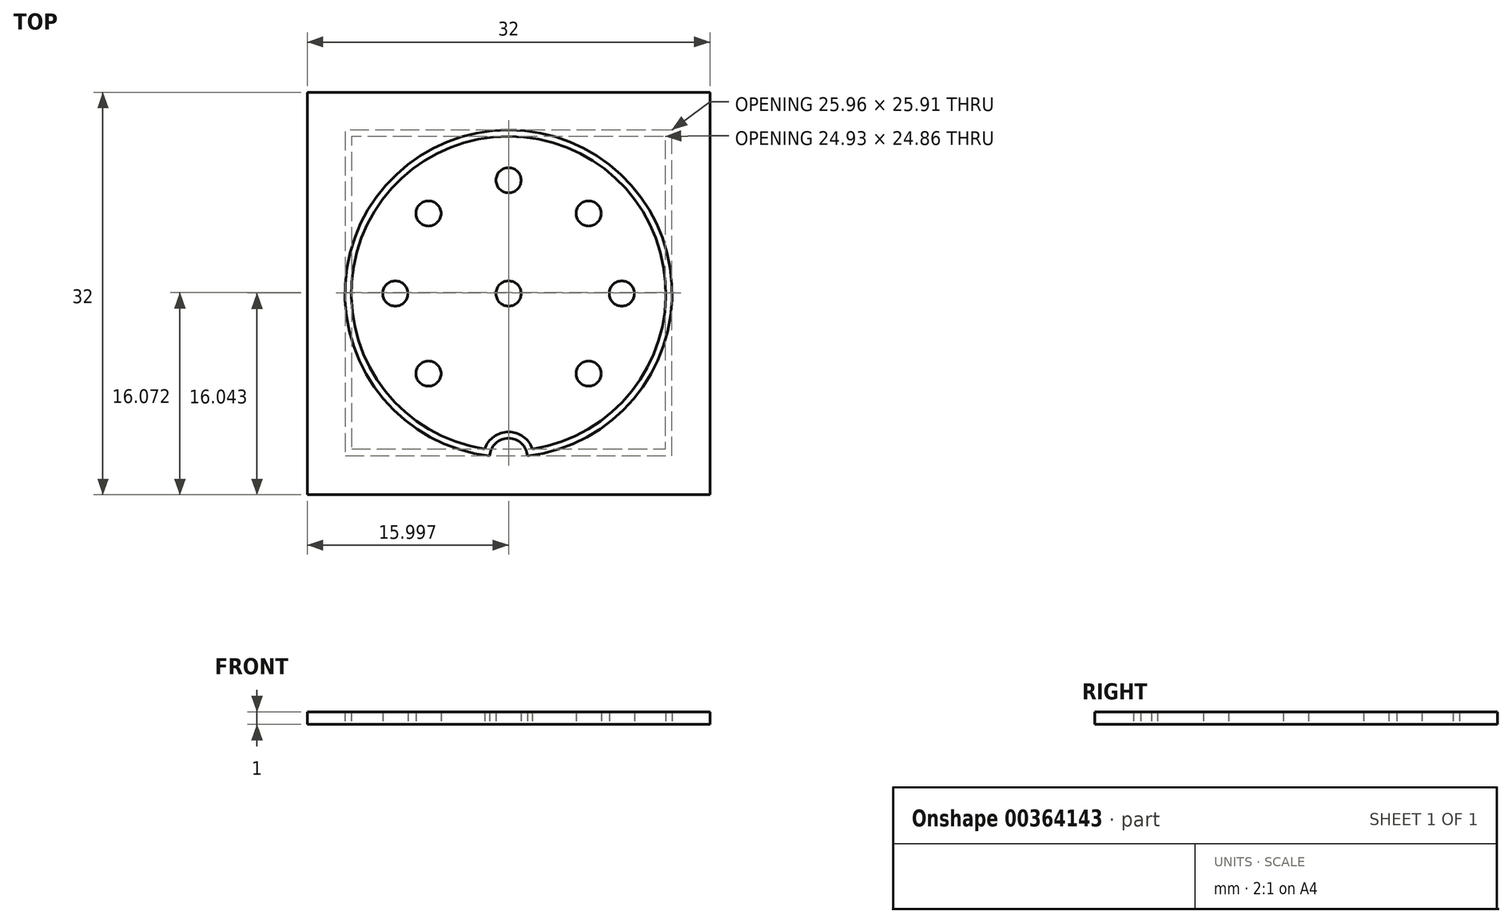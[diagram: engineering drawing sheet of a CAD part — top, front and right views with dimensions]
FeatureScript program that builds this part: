
annotation { "Feature Type Name" : "Feature", "Feature Type Description" : "" }
export const myFeature = defineFeature(function(context is Context, id is Id, definition is map)
    precondition{}
    {
        {
            var Q0;
            Q0=qCreatedBy(makeId("Top.planeOp"),FACE);
            var sketch = newSketch(context, id + "F0", { "sketchPlane" : qUnion([Q0])});
            skArc(sketch, "E0", {"start": v(1.9, -12.36) * mm, "mid": v(0, 12.5) * mm, "end": v(-1.9, -12.36) * mm});
            skCircle(sketch, "E1", {"center": v(0, 9) * mm, "radius": 1 * mm});
            skCircle(sketch, "E2", {"center": v(-9, 0) * mm, "radius": 1 * mm});
            skCircle(sketch, "E3", {"center": v(9, 0) * mm, "radius": 1 * mm});
            skLineSegment(sketch, "E4", {"start": v(0, 0) * mm, "end": v(0, 0) * mm});
            skCircle(sketch, "E5", {"center": v(-6.37, 6.36) * mm, "radius": 1 * mm});
            skCircle(sketch, "E6", {"center": v(6.36, 6.36) * mm, "radius": 1 * mm});
            skArc(sketch, "E7", {"start": v(1.5, -12.91) * mm, "mid": v(0, 13) * mm, "end": v(-1.5, -12.91) * mm});
            skArc(sketch, "E8", {"start": v(1.5, -12.91) * mm, "mid": v(0, -11.5) * mm, "end": v(-1.5, -12.91) * mm});
            skArc(sketch, "E9", {"start": v(1.9, -12.36) * mm, "mid": v(0, -11) * mm, "end": v(-1.9, -12.36) * mm});
            skCircle(sketch, "E10", {"center": v(-6.37, -6.36) * mm, "radius": 1 * mm});
            skCircle(sketch, "E11", {"center": v(6.36, -6.36) * mm, "radius": 1 * mm});
            skCircle(sketch, "E12", {"center": v(0, 0) * mm, "radius": 1 * mm});
            skLineSegment(sketch, "E13.bottom", {"start": v(16, 16) * mm, "end": v(-16, 16) * mm});
            skLineSegment(sketch, "E13.top", {"start": v(16, -16) * mm, "end": v(-16, -16) * mm});
            skLineSegment(sketch, "E13.left", {"start": v(16, 16) * mm, "end": v(16, -16) * mm});
            skLineSegment(sketch, "E13.right", {"start": v(-16, 16) * mm, "end": v(-16, -16) * mm});
            skSolve(sketch);
        }
        {
            var Q0;
            {var subQ1=sQuery(id+"F0.wireOp",EDGE,"E7");Q0=makeQuery(id+"F0.imprint","IMPRINT",FACE,{"disambiguationData":[TD([[makeQuery(id+"F0.imprint","IMPRINT",EDGE,{"derivedFrom":subQ1}),1.0]])]});}
            var Q1;
            {var subQ0=sQuery(id+"F0.wireOp",EDGE,"E1");var subQ1=makeQuery(id+"F0.imprint","INTERSECT",VERTEX,{"derivedFrom":[subQ0,sQuery(id+"F0.wireOp",EDGE,"54bc95bd-a729-4ed3-ad1b-5fd6bc5c8d13.trimOffspring")]});Q1=makeQuery(id+"F0.imprint","IMPRINT",FACE,{"disambiguationData":[TD([[makeQuery(id+"F0.imprint","IMPRINT",EDGE,{"disambiguationData":[TD([[subQ1,1.0]])],"derivedFrom":subQ0}),1.0]])]});}
            var Q2;
            {var subQ0=sQuery(id+"F0.wireOp",EDGE,"E5");var subQ1=makeQuery(id+"F0.imprint","INTERSECT",VERTEX,{"derivedFrom":[sQuery(id+"F0.wireOp",EDGE,"d5928ec5-4a45-4744-bd09-a5554664ffe6"),subQ0]});Q2=makeQuery(id+"F0.imprint","IMPRINT",FACE,{"disambiguationData":[TD([[makeQuery(id+"F0.imprint","IMPRINT",EDGE,{"disambiguationData":[TD([[subQ1,1.0]])],"derivedFrom":subQ0}),1.0]])]});}
            var Q3;
            {var subQ0=sQuery(id+"F0.wireOp",EDGE,"E2");var subQ1=makeQuery(id+"F0.imprint","INTERSECT",VERTEX,{"derivedFrom":[sQuery(id+"F0.wireOp",EDGE,"d5928ec5-4a45-4744-bd09-a5554664ffe6"),subQ0]});Q3=makeQuery(id+"F0.imprint","IMPRINT",FACE,{"disambiguationData":[TD([[makeQuery(id+"F0.imprint","IMPRINT",EDGE,{"disambiguationData":[TD([[subQ1,1.0]])],"derivedFrom":subQ0}),1.0]])]});}
            var Q4;
            {var subQ0=sQuery(id+"F0.wireOp",EDGE,"E10");var subQ1=makeQuery(id+"F0.imprint","INTERSECT",VERTEX,{"derivedFrom":[sQuery(id+"F0.wireOp",EDGE,"2c1c41d9-e77c-4c04-bfc5-bee2b52b8a49"),subQ0]});Q4=makeQuery(id+"F0.imprint","IMPRINT",FACE,{"disambiguationData":[TD([[makeQuery(id+"F0.imprint","IMPRINT",EDGE,{"disambiguationData":[TD([[subQ1,-1.0]])],"derivedFrom":subQ0}),1.0]])]});}
            var Q5;
            {var subQ0=sQuery(id+"F0.wireOp",EDGE,"E12");var subQ4=makeQuery(id+"F0.imprint","INTERSECT",VERTEX,{"derivedFrom":[sQuery(id+"F0.wireOp",EDGE,"4a31e319-3c2b-4bdd-ad33-1171a37efa25"),subQ0]});Q5=makeQuery(id+"F0.imprint","IMPRINT",FACE,{"disambiguationData":[TD([[makeQuery(id+"F0.imprint","IMPRINT",EDGE,{"disambiguationData":[TD([[subQ4,1.0]])],"derivedFrom":subQ0}),1.0]])]});}
            var Q6;
            {var subQ0=sQuery(id+"F0.wireOp",EDGE,"E6");var subQ1=makeQuery(id+"F0.imprint","INTERSECT",VERTEX,{"derivedFrom":[sQuery(id+"F0.wireOp",EDGE,"4a31e319-3c2b-4bdd-ad33-1171a37efa25"),subQ0]});Q6=makeQuery(id+"F0.imprint","IMPRINT",FACE,{"disambiguationData":[TD([[makeQuery(id+"F0.imprint","IMPRINT",EDGE,{"disambiguationData":[TD([[subQ1,1.0]])],"derivedFrom":subQ0}),1.0]])]});}
            var Q7;
            {var subQ0=sQuery(id+"F0.wireOp",EDGE,"E3");var subQ1=makeQuery(id+"F0.imprint","INTERSECT",VERTEX,{"derivedFrom":[subQ0,sQuery(id+"F0.wireOp",EDGE,"61f6ee6d-bace-4fc1-9809-4a1496155df4.trimOffspring")]});Q7=makeQuery(id+"F0.imprint","IMPRINT",FACE,{"disambiguationData":[TD([[makeQuery(id+"F0.imprint","IMPRINT",EDGE,{"disambiguationData":[TD([[subQ1,1.0]])],"derivedFrom":subQ0}),1.0]])]});}
            var Q8;
            {var subQ0=sQuery(id+"F0.wireOp",EDGE,"E11");var subQ1=makeQuery(id+"F0.imprint","INTERSECT",VERTEX,{"derivedFrom":[sQuery(id+"F0.wireOp",EDGE,"21e2062d-4835-4623-ae54-1202d8d4fc49"),subQ0]});Q8=makeQuery(id+"F0.imprint","IMPRINT",FACE,{"disambiguationData":[TD([[makeQuery(id+"F0.imprint","IMPRINT",EDGE,{"disambiguationData":[TD([[subQ1,1.0]])],"derivedFrom":subQ0}),1.0]])]});}
            var Q9;
            Q9=makeQuery(id+"F0.imprint","IMPRINT",FACE,{"disambiguationData":[TD([[makeQuery(id+"F0.imprint","IMPRINT",EDGE,{"derivedFrom":sQuery(id+"F0.wireOp",EDGE,"E10")}),1.0]])]});
            var Q10;
            Q10=makeQuery(id+"F0.imprint","IMPRINT",FACE,{"disambiguationData":[TD([[makeQuery(id+"F0.imprint","IMPRINT",EDGE,{"derivedFrom":sQuery(id+"F0.wireOp",EDGE,"E2")}),1.0]])]});
            var Q11;
            Q11=makeQuery(id+"F0.imprint","IMPRINT",FACE,{"disambiguationData":[TD([[makeQuery(id+"F0.imprint","IMPRINT",EDGE,{"derivedFrom":sQuery(id+"F0.wireOp",EDGE,"E5")}),1.0]])]});
            var Q12;
            Q12=makeQuery(id+"F0.imprint","IMPRINT",FACE,{"disambiguationData":[TD([[makeQuery(id+"F0.imprint","IMPRINT",EDGE,{"derivedFrom":sQuery(id+"F0.wireOp",EDGE,"E1")}),1.0]])]});
            var Q13;
            Q13=makeQuery(id+"F0.imprint","IMPRINT",FACE,{"disambiguationData":[TD([[makeQuery(id+"F0.imprint","IMPRINT",EDGE,{"derivedFrom":sQuery(id+"F0.wireOp",EDGE,"E6")}),1.0]])]});
            var Q14;
            Q14=makeQuery(id+"F0.imprint","IMPRINT",FACE,{"disambiguationData":[TD([[makeQuery(id+"F0.imprint","IMPRINT",EDGE,{"derivedFrom":sQuery(id+"F0.wireOp",EDGE,"E3")}),1.0]])]});
            var Q15;
            Q15=makeQuery(id+"F0.imprint","IMPRINT",FACE,{"disambiguationData":[TD([[makeQuery(id+"F0.imprint","IMPRINT",EDGE,{"derivedFrom":sQuery(id+"F0.wireOp",EDGE,"E11")}),1.0]])]});
            var Q16;
            Q16=makeQuery(id+"F0.imprint","IMPRINT",FACE,{"disambiguationData":[TD([[makeQuery(id+"F0.imprint","IMPRINT",EDGE,{"derivedFrom":sQuery(id+"F0.wireOp",EDGE,"E12")}),1.0]])]});
            extrude(context, id + "F1", {"entities" : qUnion([Q0, Q1, Q2, Q3, Q4, Q5, Q6, Q7, Q8, Q9, Q10, Q11, Q12, Q13, Q14, Q15, Q16]), "depth" : 1 * mm});
        }
        {
            var Q0;
            {var subQ1=sQuery(id+"F0.wireOp",EDGE,"E7");Q0=makeQuery(id+"F0.imprint","IMPRINT",FACE,{"disambiguationData":[TD([[makeQuery(id+"F0.imprint","IMPRINT",EDGE,{"derivedFrom":subQ1}),-1.0]])]});}
            extrude(context, id + "F2", {"entities" : qUnion([Q0]), "depth" : 1 * mm});
        }
    });
